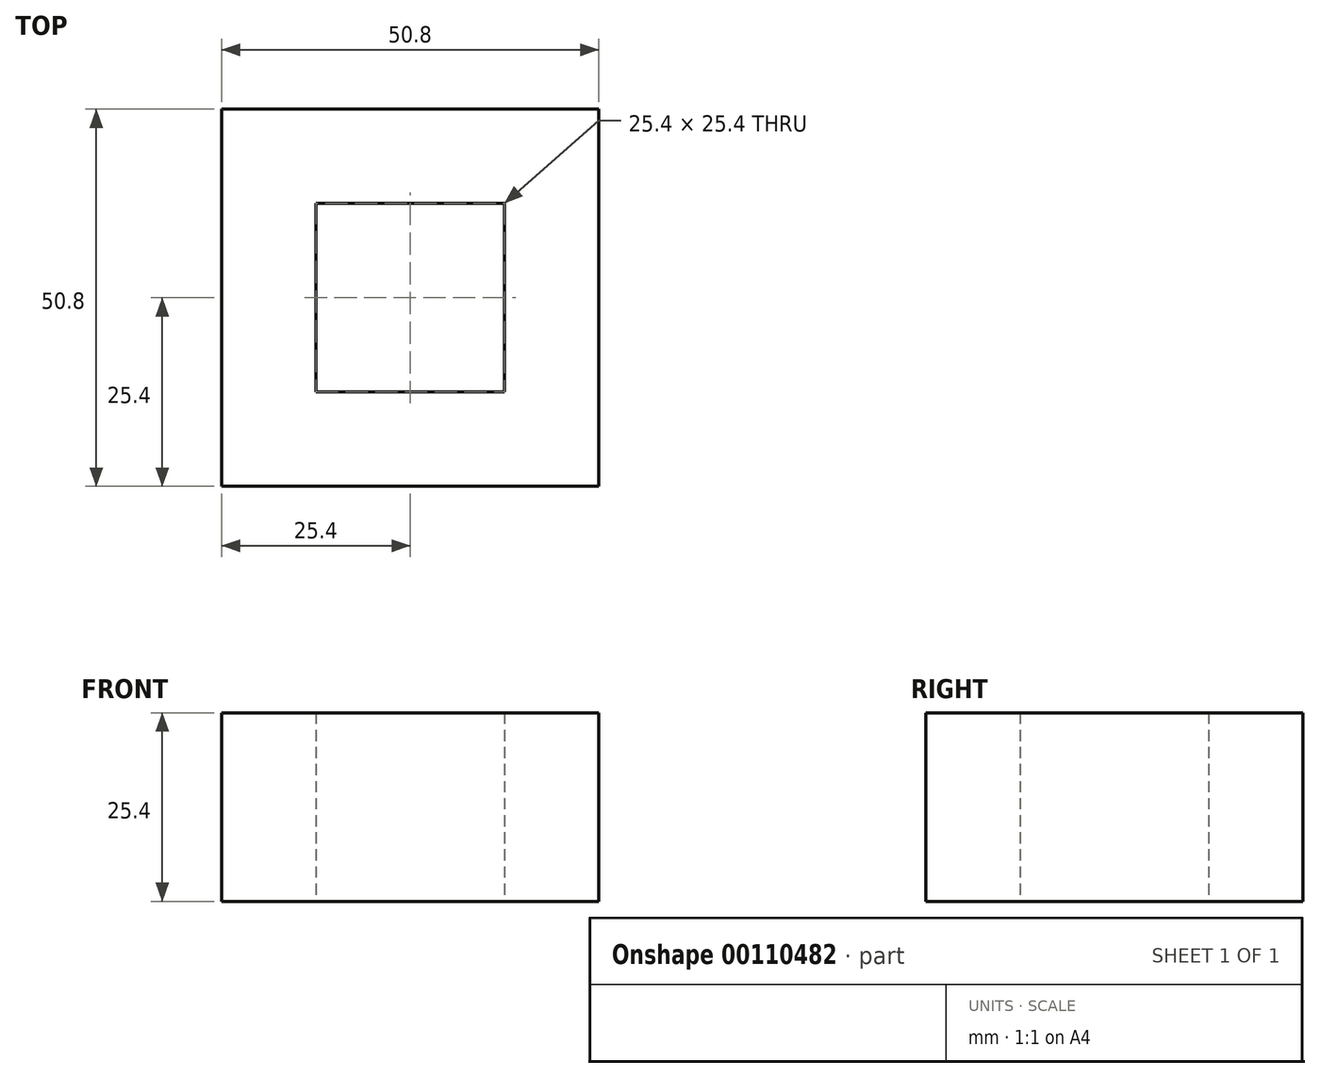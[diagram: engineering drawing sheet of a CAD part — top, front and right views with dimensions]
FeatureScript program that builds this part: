
annotation { "Feature Type Name" : "Feature", "Feature Type Description" : "" }
export const myFeature = defineFeature(function(context is Context, id is Id, definition is map)
    precondition{}
    {
        {
            var Q0;
            Q0=qCreatedBy(makeId("Top.planeOp"),FACE);
            var sketch = newSketch(context, id + "F0", { "sketchPlane" : qUnion([Q0])});
            skLineSegment(sketch, "E0.bottom", {"start": v(25.4, -25.4) * mm, "end": v(-25.4, -25.4) * mm});
            skLineSegment(sketch, "E0.top", {"start": v(25.4, 25.4) * mm, "end": v(-25.4, 25.4) * mm});
            skLineSegment(sketch, "E0.left", {"start": v(25.4, -25.4) * mm, "end": v(25.4, 25.4) * mm});
            skLineSegment(sketch, "E0.right", {"start": v(-25.4, -25.4) * mm, "end": v(-25.4, 25.4) * mm});
            skPoint(sketch, "E0.middle", {"position": v(0, 0) * mm});
            skLineSegment(sketch, "E1.bottom", {"start": v(12.7, -12.7) * mm, "end": v(-12.7, -12.7) * mm});
            skLineSegment(sketch, "E1.top", {"start": v(12.7, 12.7) * mm, "end": v(-12.7, 12.7) * mm});
            skLineSegment(sketch, "E1.left", {"start": v(12.7, -12.7) * mm, "end": v(12.7, 12.7) * mm});
            skLineSegment(sketch, "E1.right", {"start": v(-12.7, -12.7) * mm, "end": v(-12.7, 12.7) * mm});
            skSolve(sketch);
        }
        {
            var Q0;
            Q0 = qSketchRegion(id + "F0", true);
            extrude(context, id + "F1", {"entities" : qUnion([Q0]), "depth" : 25.4 * mm});
        }
    });
